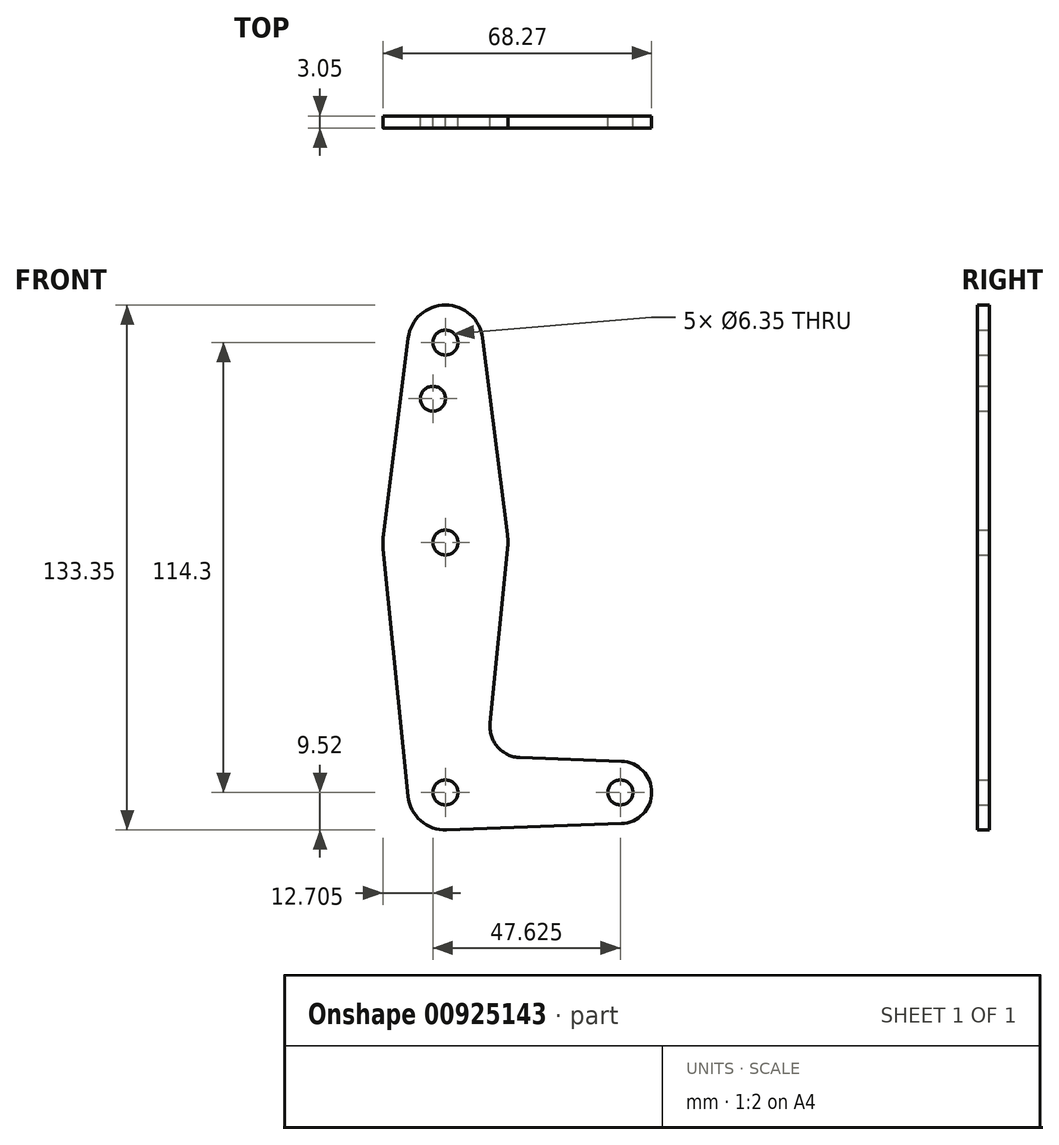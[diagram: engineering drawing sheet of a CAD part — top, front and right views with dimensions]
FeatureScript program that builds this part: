
annotation { "Feature Type Name" : "Feature", "Feature Type Description" : "" }
export const myFeature = defineFeature(function(context is Context, id is Id, definition is map)
    precondition{}
    {
        {
            var Q0;
            Q0=qCreatedBy(makeId("Front.planeOp"),FACE);
            var sketch = newSketch(context, id + "F0", { "sketchPlane" : qUnion([Q0])});
            skCircle(sketch, "E0", {"center": v(0, 0) * mm, "radius": 9.53 * mm});
            skCircle(sketch, "E1", {"center": v(0, 63.5) * mm, "radius": 15.88 * mm});
            skCircle(sketch, "E2", {"center": v(0, 114.3) * mm, "radius": 9.53 * mm});
            skCircle(sketch, "E3", {"center": v(44.45, 0) * mm, "radius": 7.94 * mm});
            skLineSegment(sketch, "E4", {"start": v(0, 114.3) * mm, "end": v(0, 0) * mm, "construction": true});
            skLineSegment(sketch, "E5", {"start": v(0, 0) * mm, "end": v(44.45, 0) * mm, "construction": true});
            skLineSegment(sketch, "E6", {"start": v(9.45, 115.5) * mm, "end": v(15.75, 65.48) * mm});
            skLineSegment(sketch, "E7", {"start": v(-9.45, 115.5) * mm, "end": v(-15.75, 65.48) * mm});
            skLineSegment(sketch, "E8", {"start": v(18.97, 8.85) * mm, "end": v(44.73, 7.93) * mm});
            skLineSegment(sketch, "E9", {"start": v(0.34, -9.52) * mm, "end": v(44.73, -7.93) * mm});
            skLineSegment(sketch, "E10", {"start": v(15.8, 61.91) * mm, "end": v(11.34, 17.6) * mm});
            skLineSegment(sketch, "E11", {"start": v(-15.8, 61.91) * mm, "end": v(-9.48, -0.95) * mm});
            skCircle(sketch, "E12", {"center": v(0, 114.3) * mm, "radius": 3.18 * mm});
            skCircle(sketch, "E13", {"center": v(-3.17, 100.03) * mm, "radius": 3.18 * mm});
            skCircle(sketch, "E14", {"center": v(0, 63.5) * mm, "radius": 3.18 * mm});
            skCircle(sketch, "E15", {"center": v(0, 0) * mm, "radius": 3.18 * mm});
            skCircle(sketch, "E16", {"center": v(44.45, 0) * mm, "radius": 3.18 * mm});
            skArc(sketch, "E17.filletArc", {"start": v(11.34, 17.6) * mm, "mid": v(13.26, 11.57) * mm, "end": v(18.97, 8.85) * mm});
            skSolve(sketch);
        }
        {
            var Q0;
            Q0 = qSketchRegion(id + "F0", true);
            extrude(context, id + "F1", {"entities" : qUnion([Q0]), "depth" : 3.05 * mm, "offsetDistance" : 25.4 * mm});
        }
    });
